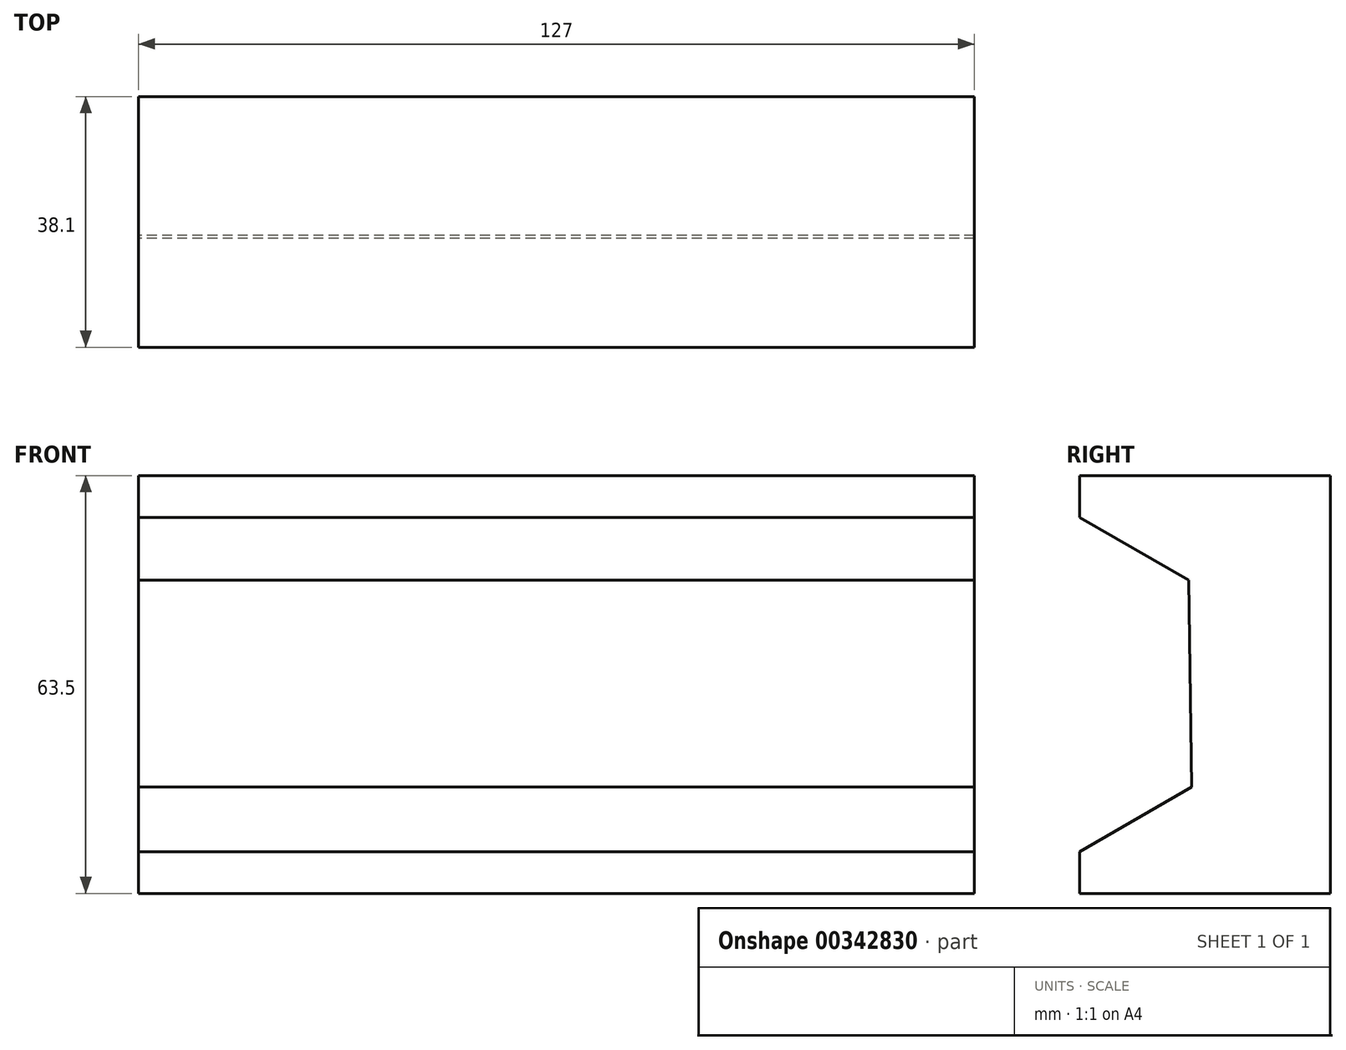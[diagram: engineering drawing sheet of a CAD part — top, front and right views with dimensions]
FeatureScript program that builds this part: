
annotation { "Feature Type Name" : "Feature", "Feature Type Description" : "" }
export const myFeature = defineFeature(function(context is Context, id is Id, definition is map)
    precondition{}
    {
        {
            var Q0;
            Q0=qCreatedBy(makeId("Right.planeOp"),FACE);
            var sketch = newSketch(context, id + "F0", { "sketchPlane" : qUnion([Q0])});
            skLineSegment(sketch, "E0", {"start": v(-9.87, 33.25) * mm, "end": v(28.23, 33.25) * mm});
            skLineSegment(sketch, "E1", {"start": v(28.23, 33.25) * mm, "end": v(28.23, -30.25) * mm});
            skLineSegment(sketch, "E2", {"start": v(28.23, -30.25) * mm, "end": v(-9.87, -30.25) * mm});
            skLineSegment(sketch, "E3", {"start": v(-9.87, -30.25) * mm, "end": v(-9.87, -23.9) * mm});
            skLineSegment(sketch, "E4", {"start": v(-9.87, 33.25) * mm, "end": v(-9.87, 26.9) * mm});
            skLineSegment(sketch, "E5", {"start": v(-9.87, -23.9) * mm, "end": v(7.14, -14.08) * mm});
            skLineSegment(sketch, "E6", {"start": v(-9.87, 26.9) * mm, "end": v(6.68, 17.35) * mm});
            skLineSegment(sketch, "E7", {"start": v(6.68, 17.35) * mm, "end": v(7.14, -14.08) * mm});
            skSolve(sketch);
        }
        {
            var Q0;
            Q0=makeQuery(id+"F0.imprint","IMPRINT",FACE,{"disambiguationData":[TD([[makeQuery(id+"F0.imprint","IMPRINT",EDGE,{"derivedFrom":sQuery(id+"F0.wireOp",EDGE,"E0")}),-1.0]])]});
            extrude(context, id + "F1", {"entities" : qUnion([Q0]), "depth" : 127 * mm});
        }
    });
